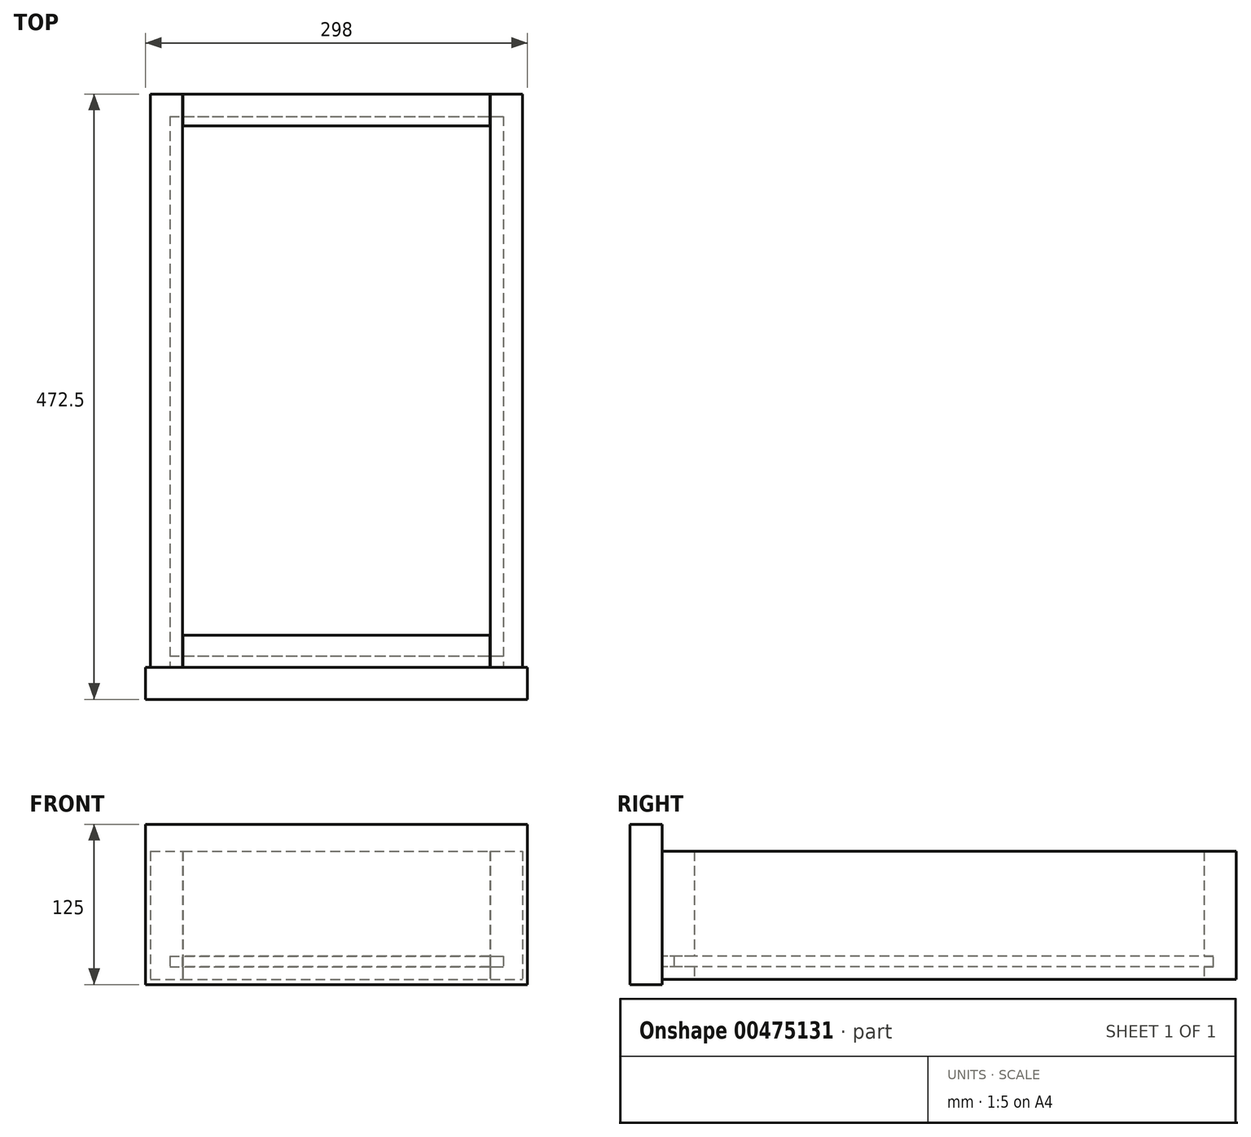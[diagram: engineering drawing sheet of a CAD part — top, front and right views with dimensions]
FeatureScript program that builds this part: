
annotation { "Feature Type Name" : "Feature", "Feature Type Description" : "" }
export const myFeature = defineFeature(function(context is Context, id is Id, definition is map)
    precondition{}
    {
        {
            var Q0;
            Q0=qCreatedBy(makeId("Top.planeOp"),FACE);
            var sketch = newSketch(context, id + "F0", { "sketchPlane" : qUnion([Q0])});
            skLineSegment(sketch, "E0.bottom", {"start": v(-296.8, -217.58) * mm, "end": v(-271.8, -217.58) * mm});
            skLineSegment(sketch, "E0.top", {"start": v(-296.8, 229.92) * mm, "end": v(-271.8, 229.92) * mm});
            skLineSegment(sketch, "E0.left", {"start": v(-296.8, -217.58) * mm, "end": v(-296.8, 229.92) * mm});
            skLineSegment(sketch, "E0.right", {"start": v(-271.8, -217.58) * mm, "end": v(-271.8, 229.92) * mm});
            skLineSegment(sketch, "E1.bottom", {"start": v(-31.8, 229.92) * mm, "end": v(-6.8, 229.92) * mm});
            skLineSegment(sketch, "E1.top", {"start": v(-31.8, -217.58) * mm, "end": v(-6.8, -217.58) * mm});
            skLineSegment(sketch, "E1.left", {"start": v(-31.8, 229.92) * mm, "end": v(-31.8, -217.58) * mm});
            skLineSegment(sketch, "E1.right", {"start": v(-6.8, 229.92) * mm, "end": v(-6.8, -217.58) * mm});
            skLineSegment(sketch, "E2.bottom", {"start": v(-271.6, 229.92) * mm, "end": v(-32, 229.92) * mm});
            skLineSegment(sketch, "E2.top", {"start": v(-271.6, 204.92) * mm, "end": v(-32, 204.92) * mm});
            skLineSegment(sketch, "E2.left", {"start": v(-271.6, 229.92) * mm, "end": v(-271.6, 204.92) * mm});
            skLineSegment(sketch, "E2.right", {"start": v(-32, 229.92) * mm, "end": v(-32, 204.92) * mm});
            skLineSegment(sketch, "E3.bottom", {"start": v(-271.6, -217.58) * mm, "end": v(-32, -217.58) * mm});
            skLineSegment(sketch, "E3.top", {"start": v(-271.6, -192.58) * mm, "end": v(-32, -192.58) * mm});
            skLineSegment(sketch, "E3.left", {"start": v(-271.6, -217.58) * mm, "end": v(-271.6, -192.58) * mm});
            skLineSegment(sketch, "E3.right", {"start": v(-32, -217.58) * mm, "end": v(-32, -192.58) * mm});
            skSolve(sketch);
        }
        {
            var Q0;
            Q0 = qSketchRegion(id + "F0", true);
            extrude(context, id + "F1", {"entities" : qUnion([Q0]), "depth" : 100 * mm, "offsetDistance" : 25 * mm});
        }
        {
            var Q0;
            Q0=makeQuery(id+"F1.opExtrude","SWEPT_FACE",FACE,{"disambiguationData":[OSD([sQuery(id+"F0.wireOp",EDGE,"E0.bottom")])]});
            var sketch = newSketch(context, id + "F2", { "sketchPlane" : qUnion([Q0])});
            skLineSegment(sketch, "E4.bottom", {"start": v(-281.8, 18) * mm, "end": v(-21.8, 18) * mm});
            skLineSegment(sketch, "E4.top", {"start": v(-281.8, 10) * mm, "end": v(-21.8, 10) * mm});
            skLineSegment(sketch, "E4.left", {"start": v(-281.8, 18) * mm, "end": v(-281.8, 10) * mm});
            skLineSegment(sketch, "E4.right", {"start": v(-21.8, 18) * mm, "end": v(-21.8, 10) * mm});
            skSolve(sketch);
        }
        {
            var Q0;
            Q0 = qSketchRegion(id + "F2", true);
            extrude(context, id + "F3", {"entities" : qUnion([Q0]), "operationType" : NewBodyOperationType.REMOVE, "oppositeDirection" : true, "depth" : 430 * mm, "offsetDistance" : 25 * mm});
        }
        {
            var Q0;
            {var subQ1=sQuery(id+"F2.wireOp",EDGE,"E4.top");Q0=makeQuery(id+"F3.boolean.opBoolean","COPY",FACE,{"disambiguationData":[TD([makeQuery(id+"F1.opExtrude","SWEPT_FACE",FACE,{"disambiguationData":[OSD([sQuery(id+"F0.wireOp",EDGE,"E0.bottom")])]})])],"derivedFrom":makeQuery(id+"F3.opExtrude","SWEPT_FACE",FACE,{"disambiguationData":[OSD([subQ1])]})});}
            var sketch = newSketch(context, id + "F4", { "sketchPlane" : qUnion([Q0])});
            skLineSegment(sketch, "E5.bottom", {"start": v(-281.8, 212.42) * mm, "end": v(-21.8, 212.42) * mm});
            skLineSegment(sketch, "E5.top", {"start": v(-281.8, -208.51) * mm, "end": v(-21.8, -208.51) * mm});
            skLineSegment(sketch, "E5.left", {"start": v(-281.8, 212.42) * mm, "end": v(-281.8, -208.51) * mm});
            skLineSegment(sketch, "E5.right", {"start": v(-21.8, 212.42) * mm, "end": v(-21.8, -208.51) * mm});
            skSolve(sketch);
        }
        {
            var Q0;
            Q0 = qSketchRegion(id + "F4", true);
            extrude(context, id + "F5", {"entities" : qUnion([Q0]), "depth" : 8 * mm, "offsetDistance" : 25 * mm});
        }
        {
            var Q0;
            Q0=makeQuery(id+"F1.opExtrude","SWEPT_FACE",FACE,{"disambiguationData":[OSD([sQuery(id+"F0.wireOp",EDGE,"E0.bottom")])]});
            var sketch = newSketch(context, id + "F6", { "sketchPlane" : qUnion([Q0])});
            skLineSegment(sketch, "E6.bottom", {"start": v(-300.8, -4) * mm, "end": v(-2.8, -4) * mm});
            skLineSegment(sketch, "E6.top", {"start": v(-300.8, 121) * mm, "end": v(-2.8, 121) * mm});
            skLineSegment(sketch, "E6.left", {"start": v(-300.8, -4) * mm, "end": v(-300.8, 121) * mm});
            skLineSegment(sketch, "E6.right", {"start": v(-2.8, -4) * mm, "end": v(-2.8, 121) * mm});
            skSolve(sketch);
        }
        {
            var Q0;
            Q0 = qSketchRegion(id + "F6", true);
            extrude(context, id + "F7", {"entities" : qUnion([Q0]), "depth" : 25 * mm, "offsetDistance" : 25 * mm});
        }
    });
